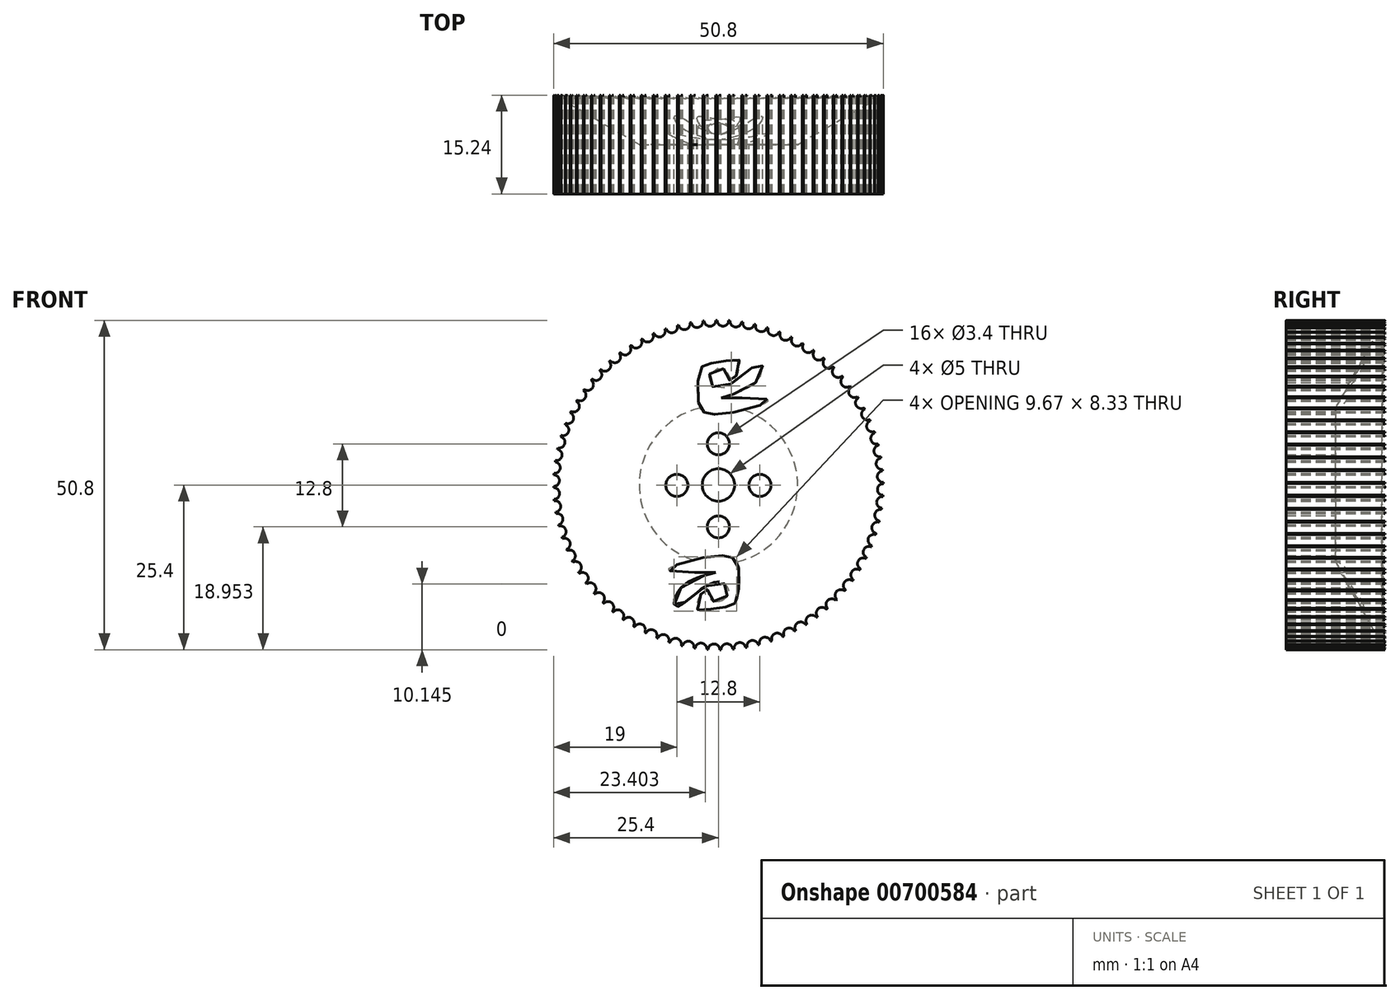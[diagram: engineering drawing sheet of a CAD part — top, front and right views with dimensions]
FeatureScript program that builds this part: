
annotation { "Feature Type Name" : "Feature", "Feature Type Description" : "" }
export const myFeature = defineFeature(function(context is Context, id is Id, definition is map)
    precondition{}
    {
        {
            var Q0;
            Q0=qCreatedBy(makeId("Front.planeOp"),FACE);
            var sketch = newSketch(context, id + "F0", { "sketchPlane" : qUnion([Q0])});
            skCircle(sketch, "E0", {"center": v(0, 0) * mm, "radius": 25.4 * mm});
            skCircle(sketch, "E1", {"center": v(0, 0) * mm, "radius": 2.5 * mm});
            skCircle(sketch, "E2", {"center": v(0, 6.35) * mm, "radius": 1.7 * mm});
            skCircle(sketch, "E3", {"center": v(6.4, -0.05) * mm, "radius": 1.7 * mm});
            skCircle(sketch, "E4", {"center": v(0, -6.45) * mm, "radius": 1.7 * mm});
            skCircle(sketch, "E5", {"center": v(-6.4, -0.05) * mm, "radius": 1.7 * mm});
            skSolve(sketch);
        }
        {
            var Q0;
            Q0 = qSketchRegion(id + "F0", true);
            extrude(context, id + "F1", {"entities" : qUnion([Q0]), "depth" : 15.24 * mm, "offsetDistance" : 25.4 * mm});
        }
        {
            var Q0;
            Q0=makeQuery(id+"F0.imprint","IMPRINT",FACE,{"disambiguationData":[TD([[makeQuery(id+"F0.imprint","IMPRINT",EDGE,{"derivedFrom":sQuery(id+"F0.wireOp",EDGE,"E0")}),1.0]])]});
            var Q1;
            Q1=makeQuery(id+"F0.imprint","IMPRINT",FACE,{"disambiguationData":[TD([[makeQuery(id+"F0.imprint","IMPRINT",EDGE,{"derivedFrom":sQuery(id+"F0.wireOp",EDGE,"E5")}),1.0]])]});
            var Q2;
            Q2=makeQuery(id+"F0.imprint","IMPRINT",FACE,{"disambiguationData":[TD([[makeQuery(id+"F0.imprint","IMPRINT",EDGE,{"derivedFrom":sQuery(id+"F0.wireOp",EDGE,"E3")}),1.0]])]});
            var Q3;
            Q3=makeQuery(id+"F0.imprint","IMPRINT",FACE,{"disambiguationData":[TD([[makeQuery(id+"F0.imprint","IMPRINT",EDGE,{"derivedFrom":sQuery(id+"F0.wireOp",EDGE,"E2")}),1.0]])]});
            var Q4;
            Q4=makeQuery(id+"F0.imprint","IMPRINT",FACE,{"disambiguationData":[TD([[makeQuery(id+"F0.imprint","IMPRINT",EDGE,{"derivedFrom":sQuery(id+"F0.wireOp",EDGE,"E4")}),1.0]])]});
            var Q5;
            Q5=makeQuery(id+"F0.imprint","IMPRINT",FACE,{"disambiguationData":[TD([[makeQuery(id+"F0.imprint","IMPRINT",EDGE,{"derivedFrom":sQuery(id+"F0.wireOp",EDGE,"E1")}),1.0]])]});
            extrude(context, id + "F2", {"entities" : qUnion([Q0, Q1, Q2, Q3, Q4, Q5]), "operationType" : NewBodyOperationType.REMOVE, "depth" : 7.62 * mm, "offsetDistance" : 25.4 * mm, "hasDraft" : true, "draftAngle" : 60 * degree, "draftPullDirection" : true});
        }
        {
            var Q0;
            Q0=qCreatedBy(makeId("Front.planeOp"),FACE);
            var sketch = newSketch(context, id + "F3", { "sketchPlane" : qUnion([Q0])});
            skFitSpline(sketch, "E6", {"points": [v(0.43, 13.47) * mm, v(7.67, 13.14) * mm, v(1.54, 11.06) * mm, v(-1.72, 11.06) * mm, v(-2.9, 11.9) * mm, v(-2.9, 17.51) * mm, v(-1.91, 18.62) * mm, v(0.82, 19.08) * mm, v(3.3, 19.08) * mm, v(1.93, 15.82) * mm, v(1.09, 17.77) * mm, v(-1.52, 16.8) * mm, v(0.24, 14.9) * mm, v(6.5, 18.75) * mm, v(5.32, 15.43) * mm, v(0.43, 13.47) * mm]});
            skSolve(sketch);
        }
        {
            var Q0;
            Q0 = qSketchRegion(id + "F3", true);
            extrude(context, id + "F4", {"entities" : qUnion([Q0]), "depth" : 25.4 * mm, "offsetDistance" : 25.4 * mm});
        }
        {
            var Q0;
            Q0=qCreatedBy(makeId("Top.planeOp"),FACE);
            var sketch = newSketch(context, id + "F5", { "sketchPlane" : qUnion([Q0])});
            skLineSegment(sketch, "E7", {"start": v(0, 35.49) * mm, "end": v(0, -33.64) * mm});
            skSolve(sketch);
        }
        {
            var Q0;
            Q0=makeQuery(id+"F4.opExtrude","SWEPT_BODY",BODY,{"disambiguationData":[OSD([sQuery(id+"F3.wireOp",EDGE,"E6")])]});
            var Q1;
            Q1=sQuery(id+"F5.wireOp",EDGE,"E7");
            circularPattern(context, id + "F6", {"operationType" : NewBodyOperationType.REMOVE, "entities" : qUnion([Q0]), "axis" : qUnion([Q1]), "angle" : 360 * degree, "instanceCount" : 2, "oppositeDirection" : true, "equalSpace" : true});
        }
        {
            var Q0;
            Q0=makeQuery(id+"F1.opExtrude","CAP_FACE",FACE,{"disambiguationData":[OSD([sQuery(id+"F0.wireOp",EDGE,"E0"),sQuery(id+"F0.wireOp",EDGE,"E1"),sQuery(id+"F0.wireOp",EDGE,"E2"),sQuery(id+"F0.wireOp",EDGE,"E3"),sQuery(id+"F0.wireOp",EDGE,"E4"),sQuery(id+"F0.wireOp",EDGE,"E5")])],"isStart":false});
            var sketch = newSketch(context, id + "F7", { "sketchPlane" : qUnion([Q0])});
            skCircle(sketch, "E8", {"center": v(-10.92, 22.93) * mm, "radius": 0.89 * mm});
            skSolve(sketch);
        }
        {
            var Q0;
            Q0 = qSketchRegion(id + "F7", true);
            extrude(context, id + "F8", {"entities" : qUnion([Q0]), "endBound" : BoundingType.SYMMETRIC, "depth" : 50.8 * mm, "offsetDistance" : 25.4 * mm});
        }
        {
            var Q0;
            Q0=makeQuery(id+"F8.opExtrude","SWEPT_BODY",BODY,{"disambiguationData":[OSD([sQuery(id+"F7.wireOp",EDGE,"E8")])]});
            var Q1;
            Q1=sQuery(id+"F5.wireOp",EDGE,"E7");
            circularPattern(context, id + "F9", {"operationType" : NewBodyOperationType.REMOVE, "entities" : qUnion([Q0]), "axis" : qUnion([Q1]), "angle" : 360 * degree, "instanceCount" : 80, "equalSpace" : true});
        }
    });
